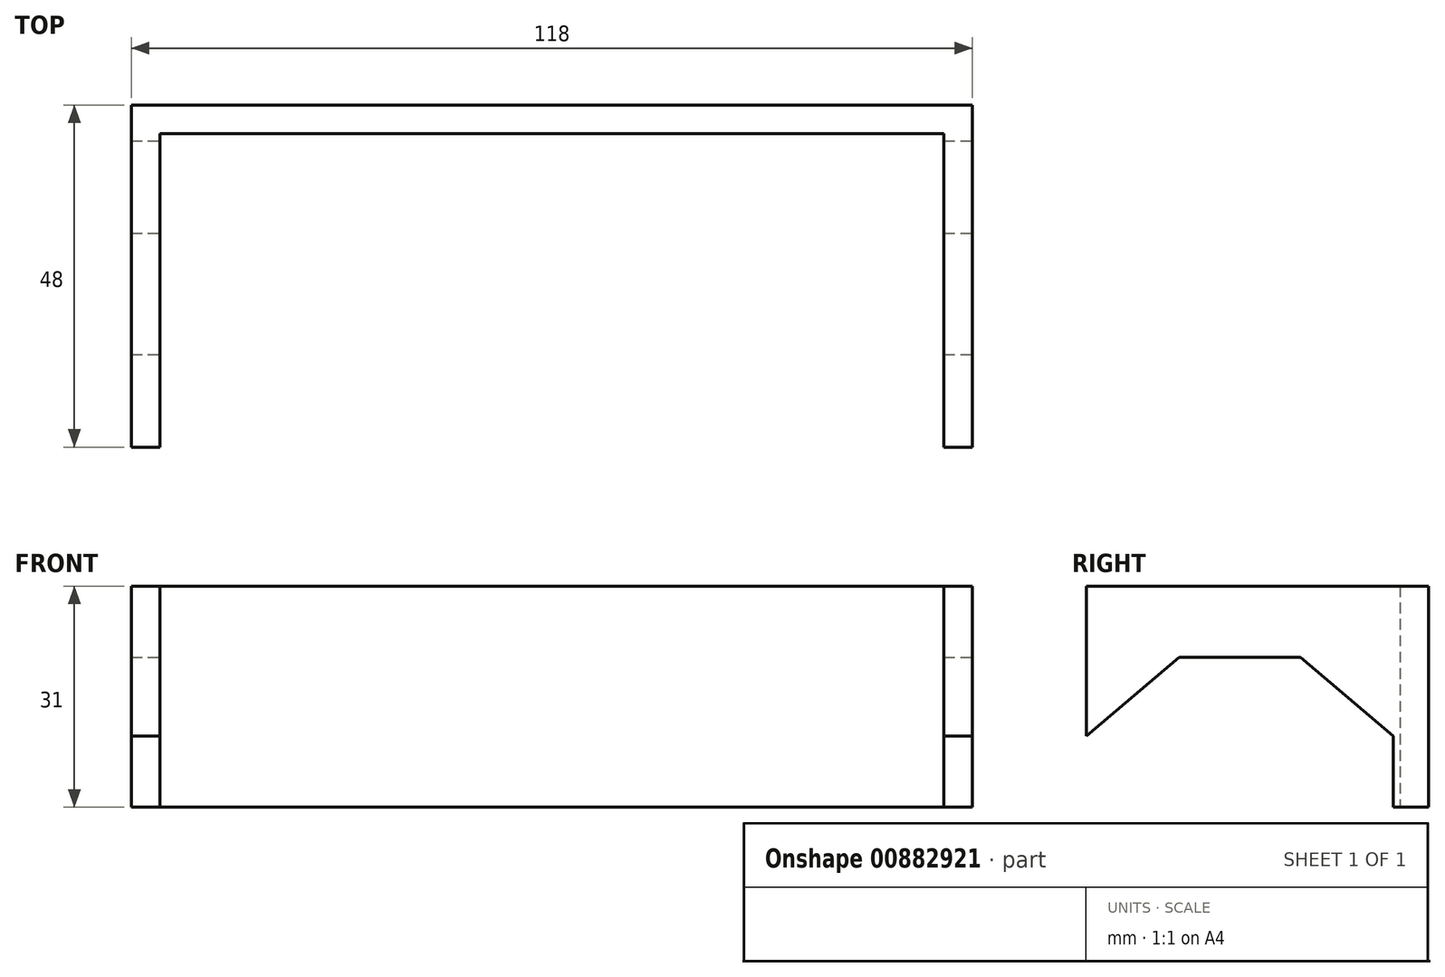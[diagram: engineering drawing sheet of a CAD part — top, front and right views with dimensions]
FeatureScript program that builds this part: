
annotation { "Feature Type Name" : "Feature", "Feature Type Description" : "" }
export const myFeature = defineFeature(function(context is Context, id is Id, definition is map)
    precondition{}
    {
        {
            var Q0;
            Q0=qCreatedBy(makeId("Top.planeOp"),FACE);
            var sketch = newSketch(context, id + "F0", { "sketchPlane" : qUnion([Q0])});
            skLineSegment(sketch, "E0.bottom", {"start": v(55, -22) * mm, "end": v(-55, -22) * mm});
            skLineSegment(sketch, "E0.top", {"start": v(55, 22) * mm, "end": v(-55, 22) * mm});
            skLineSegment(sketch, "E0.left", {"start": v(55, -22) * mm, "end": v(55, 22) * mm});
            skLineSegment(sketch, "E0.right", {"start": v(-55, -22) * mm, "end": v(-55, 22) * mm});
            skPoint(sketch, "E0.middle", {"position": v(0, 0) * mm});
            skSolve(sketch);
        }
        {
            var Q0;
            Q0=makeQuery(id+"F0.imprint","IMPRINT",FACE,{"disambiguationData":[TD([[makeQuery(id+"F0.imprint","IMPRINT",EDGE,{"derivedFrom":sQuery(id+"F0.wireOp",EDGE,"E0.bottom")}),-1.0]])]});
            extrude(context, id + "F1", {"entities" : qUnion([Q0]), "depth" : 21 * mm, "offsetDistance" : 25.4 * mm});
        }
        {
            var Q0;
            Q0=makeQuery(id+"F1.opExtrude","SWEPT_BODY",BODY,{"disambiguationData":[OSD([sQuery(id+"F0.wireOp",EDGE,"E0.bottom"),sQuery(id+"F0.wireOp",EDGE,"E0.top"),sQuery(id+"F0.wireOp",EDGE,"E0.left"),sQuery(id+"F0.wireOp",EDGE,"E0.right")])]});
            deleteBodies(context, id + "F2", {"entities" : qUnion([Q0])});
        }
        {
            var Q0;
            Q0=qCreatedBy(makeId("Right.planeOp"),FACE);
            cPlane(context, id + "F3", {"entities" : qUnion([Q0]), "cplaneType" : CPlaneType.OFFSET, "offset" : 59 * mm, "width" : 152.4 * mm, "height" : 152.4 * mm});
        }
        {
            var Q0;
            Q0=qCreatedBy(id+"F3.planeOp",FACE);
            var sketch = newSketch(context, id + "F4", { "sketchPlane" : qUnion([Q0])});
            skLineSegment(sketch, "E1.bottom", {"start": v(21.5, 5.09) * mm, "end": v(-21.5, 5.09) * mm});
            skLineSegment(sketch, "E1.top", {"start": v(21.5, -15.91) * mm, "end": v(-21.5, -15.91) * mm});
            skLineSegment(sketch, "E1.left", {"start": v(21.5, 5.09) * mm, "end": v(21.5, -15.91) * mm});
            skLineSegment(sketch, "E1.right", {"start": v(-21.5, 5.09) * mm, "end": v(-21.5, -15.91) * mm});
            skPoint(sketch, "E1.middle", {"position": v(0, -5.41) * mm});
            skSolve(sketch);
        }
        {
            var Q0;
            Q0=makeQuery(id+"F4.imprint","IMPRINT",FACE,{"disambiguationData":[TD([[makeQuery(id+"F4.imprint","IMPRINT",EDGE,{"derivedFrom":sQuery(id+"F4.wireOp",EDGE,"E1.bottom")}),1.0]])]});
            extrude(context, id + "F5", {"entities" : qUnion([Q0]), "oppositeDirection" : true, "depth" : 118 * mm, "offsetDistance" : 25.4 * mm});
        }
        {
            var Q0;
            Q0=makeQuery(id+"F5.opExtrude","SWEPT_FACE",FACE,{"disambiguationData":[OSD([sQuery(id+"F4.wireOp",EDGE,"E1.bottom")])]});
            extrude(context, id + "F6", {"entities" : qUnion([Q0]), "operationType" : NewBodyOperationType.ADD, "depth" : 10 * mm, "offsetDistance" : 25.4 * mm});
        }
        {
            var Q0;
            {var subQ0=sQuery(id+"F4.wireOp",EDGE,"E1.left");Q0=makeQuery(id+"F6.boolean.opBoolean","MERGE",FACE,{"derivedFrom":[makeQuery(id+"F5.opExtrude","SWEPT_FACE",FACE,{"disambiguationData":[OSD([subQ0])]}),makeQuery(id+"F6.opExtrude","SWEPT_FACE",FACE,{"disambiguationData":[OSD([sQuery(id+"F4.wireOp",EDGE,"E1.bottom"),subQ0])]})]});}
            extrude(context, id + "F7", {"entities" : qUnion([Q0]), "operationType" : NewBodyOperationType.ADD, "depth" : 5 * mm, "offsetDistance" : 25.4 * mm});
        }
        {
            var Q0;
            Q0=makeQuery(id+"F5.opExtrude","CAP_FACE",FACE,{"disambiguationData":[OSD([sQuery(id+"F4.wireOp",EDGE,"E1.bottom"),sQuery(id+"F4.wireOp",EDGE,"E1.top"),sQuery(id+"F4.wireOp",EDGE,"E1.left"),sQuery(id+"F4.wireOp",EDGE,"E1.right")])],"isStart":true});
            var sketch = newSketch(context, id + "F8", { "sketchPlane" : qUnion([Q0])});
            skLineSegment(sketch, "E2", {"start": v(-21.5, -15.91) * mm, "end": v(-21.5, -5.91) * mm});
            skLineSegment(sketch, "E3", {"start": v(-21.5, -5.91) * mm, "end": v(21.5, -5.91) * mm});
            skLineSegment(sketch, "E4", {"start": v(21.5, -5.91) * mm, "end": v(21.5, -15.91) * mm});
            skLineSegment(sketch, "E5", {"start": v(21.5, -15.91) * mm, "end": v(21.5, -5.91) * mm});
            skLineSegment(sketch, "E6", {"start": v(0, -5.91) * mm, "end": v(0, 5.09) * mm});
            skLineSegment(sketch, "E7", {"start": v(0, 5.09) * mm, "end": v(8.5, 5.09) * mm});
            skLineSegment(sketch, "E8", {"start": v(8.5, 5.09) * mm, "end": v(-8.5, 5.09) * mm});
            skLineSegment(sketch, "E9", {"start": v(-8.5, 5.09) * mm, "end": v(-21.5, -5.91) * mm});
            skLineSegment(sketch, "E10", {"start": v(8.5, 5.09) * mm, "end": v(21.5, -5.91) * mm});
            skLineSegment(sketch, "E11", {"start": v(-8.5, 5.09) * mm, "end": v(-8.5, 15.09) * mm});
            skLineSegment(sketch, "E12", {"start": v(-8.5, 15.09) * mm, "end": v(-8.5, 5.09) * mm});
            skLineSegment(sketch, "E13", {"start": v(8.5, 5.09) * mm, "end": v(8.5, 15.09) * mm});
            skLineSegment(sketch, "E14", {"start": v(8.5, 15.09) * mm, "end": v(21.5, 5.09) * mm});
            skLineSegment(sketch, "E15", {"start": v(21.5, 5.09) * mm, "end": v(8.5, 15.09) * mm});
            skLineSegment(sketch, "E16", {"start": v(-8.5, 15.09) * mm, "end": v(-21.5, 5.09) * mm});
            skLineSegment(sketch, "E17", {"start": v(-21.5, 5.09) * mm, "end": v(-8.5, 15.09) * mm});
            skLineSegment(sketch, "E18", {"start": v(-8.5, 15.09) * mm, "end": v(8.5, 15.09) * mm});
            skLineSegment(sketch, "E19", {"start": v(21.5, 5.09) * mm, "end": v(26.5, 5.09) * mm});
            skLineSegment(sketch, "E20", {"start": v(21.5, -5.91) * mm, "end": v(26.5, -5.91) * mm});
            skSolve(sketch);
        }
        {
            var Q0;
            {var subQ0=sQuery(id+"F4.wireOp",EDGE,"E1.top");Q0=makeQuery(id+"F7.boolean.opBoolean","MERGE",FACE,{"derivedFrom":[makeQuery(id+"F5.opExtrude","SWEPT_FACE",FACE,{"disambiguationData":[OSD([subQ0])]}),makeQuery(id+"F7.opExtrude","SWEPT_FACE",FACE,{"disambiguationData":[OSD([subQ0,sQuery(id+"F4.wireOp",EDGE,"E1.left")])]})]});}
            shell(context, id + "F9", {"entities" : qUnion([Q0]), "thickness" : 4 * mm});
        }
        {
            var Q0;
            {var subQ0=sQuery(id+"F4.wireOp",EDGE,"E1.left");var subQ1=sQuery(id+"F4.wireOp",EDGE,"E1.bottom");Q0=makeQuery(id+"F9.opShell","OFFSET_FACE",FACE,{"disambiguationData":[OSD([subQ1,subQ0]),TDD([makeQuery(id+"F7.boolean.opBoolean","MERGE",FACE,{"derivedFrom":[makeQuery(id+"F6.opExtrude","CAP_FACE",FACE,{"disambiguationData":[OSD([subQ1])],"isStart":false}),makeQuery(id+"F7.opExtrude","SWEPT_FACE",FACE,{"disambiguationData":[OSD([subQ1,subQ0]),TDD([makeQuery(id+"F6.opExtrude","CAP_EDGE",EDGE,{"disambiguationData":[OSD([subQ1,subQ0])],"isStart":false})])]})]})])]});}
            extrude(context, id + "F10", {"entities" : qUnion([Q0]), "operationType" : NewBodyOperationType.REMOVE, "oppositeDirection" : true, "depth" : 25.4 * mm, "offsetDistance" : 25.4 * mm});
        }
        {
            var Q0;
            {var subQ2=sQuery(id+"F8.wireOp",EDGE,"E6");Q0=makeQuery(id+"F8.imprint","IMPRINT",FACE,{"disambiguationData":[TD([[makeQuery(id+"F8.imprint","IMPRINT",EDGE,{"derivedFrom":subQ2}),-1.0]])]});}
            var Q1;
            {var subQ3=sQuery(id+"F8.wireOp",EDGE,"E2");Q1=makeQuery(id+"F8.imprint","IMPRINT",FACE,{"disambiguationData":[TD([[makeQuery(id+"F8.imprint","IMPRINT",EDGE,{"derivedFrom":subQ3}),1.0]])]});}
            var Q2;
            {var subQ0=sQuery(id+"F8.wireOp",EDGE,"E5");Q2=makeQuery(id+"F8.imprint","IMPRINT",FACE,{"disambiguationData":[TD([[makeQuery(id+"F8.imprint","IMPRINT",EDGE,{"derivedFrom":subQ0}),-1.0]])]});}
            var Q3;
            {var subQ0=sQuery(id+"F8.wireOp",EDGE,"E15");Q3=makeQuery(id+"F8.imprint","IMPRINT",FACE,{"disambiguationData":[TD([[makeQuery(id+"F8.imprint","IMPRINT",EDGE,{"derivedFrom":subQ0}),-1.0]])]});}
            var Q4;
            {var subQ4=sQuery(id+"F8.wireOp",EDGE,"E6");Q4=makeQuery(id+"F8.imprint","IMPRINT",FACE,{"disambiguationData":[TD([[makeQuery(id+"F8.imprint","IMPRINT",EDGE,{"derivedFrom":subQ4}),1.0]])]});}
            var Q5;
            {var subQ0=sQuery(id+"F8.wireOp",EDGE,"E17");Q5=makeQuery(id+"F8.imprint","IMPRINT",FACE,{"disambiguationData":[TD([[makeQuery(id+"F8.imprint","IMPRINT",EDGE,{"derivedFrom":subQ0}),1.0]])]});}
            extrude(context, id + "F11", {"entities" : qUnion([Q0, Q1, Q2, Q3, Q4, Q5]), "operationType" : NewBodyOperationType.REMOVE, "oppositeDirection" : true, "depth" : 254 * mm, "offsetDistance" : 25.4 * mm});
        }
        {
            var Q0;
            {var subQ0=sQuery(id+"F4.wireOp",EDGE,"E1.right");var subQ1=sQuery(id+"F4.wireOp",EDGE,"E1.bottom");Q0=makeQuery(id+"F10.boolean.opBoolean","MERGE",FACE,{"derivedFrom":[makeQuery(id+"F9.opShell","OFFSET_FACE",FACE,{"disambiguationData":[OSD([subQ1,subQ0])]})],"fromTools":[makeQuery(id+"F10.opExtrude","SWEPT_FACE",FACE,{"disambiguationData":[OSD([subQ1,subQ0])]})]});}
            extrude(context, id + "F12", {"entities" : qUnion([Q0]), "operationType" : NewBodyOperationType.REMOVE, "oppositeDirection" : true, "depth" : 25.4 * mm, "offsetDistance" : 25.4 * mm});
        }
        {
            var Q0;
            Q0=makeQuery(id+"F11.boolean.opBoolean","COPY",FACE,{"derivedFrom":makeQuery(id+"F11.opExtrude","SWEPT_FACE",FACE,{"disambiguationData":[OSD([sQuery(id+"F8.wireOp",EDGE,"E9")])]})});
            var sketch = newSketch(context, id + "F13", { "sketchPlane" : qUnion([Q0])});
            skLineSegment(sketch, "E21", {"start": v(55, 15) * mm, "end": v(55, 20.23) * mm});
            skLineSegment(sketch, "E22", {"start": v(-55, 15) * mm, "end": v(-55, 20.23) * mm});
            skSolve(sketch);
        }
        {
            var Q0;
            {var subQ0=sQuery(id+"F13.wireOp",EDGE,"E21");Q0=makeQuery(id+"F13.imprint","IMPRINT",FACE,{"disambiguationData":[TD([[makeQuery(id+"F13.imprint","IMPRINT",EDGE,{"derivedFrom":subQ0}),1.0]])]});}
            extrude(context, id + "F14", {"entities" : qUnion([Q0]), "operationType" : NewBodyOperationType.REMOVE, "oppositeDirection" : true, "depth" : 25.4 * mm, "offsetDistance" : 25.4 * mm});
        }
    });
